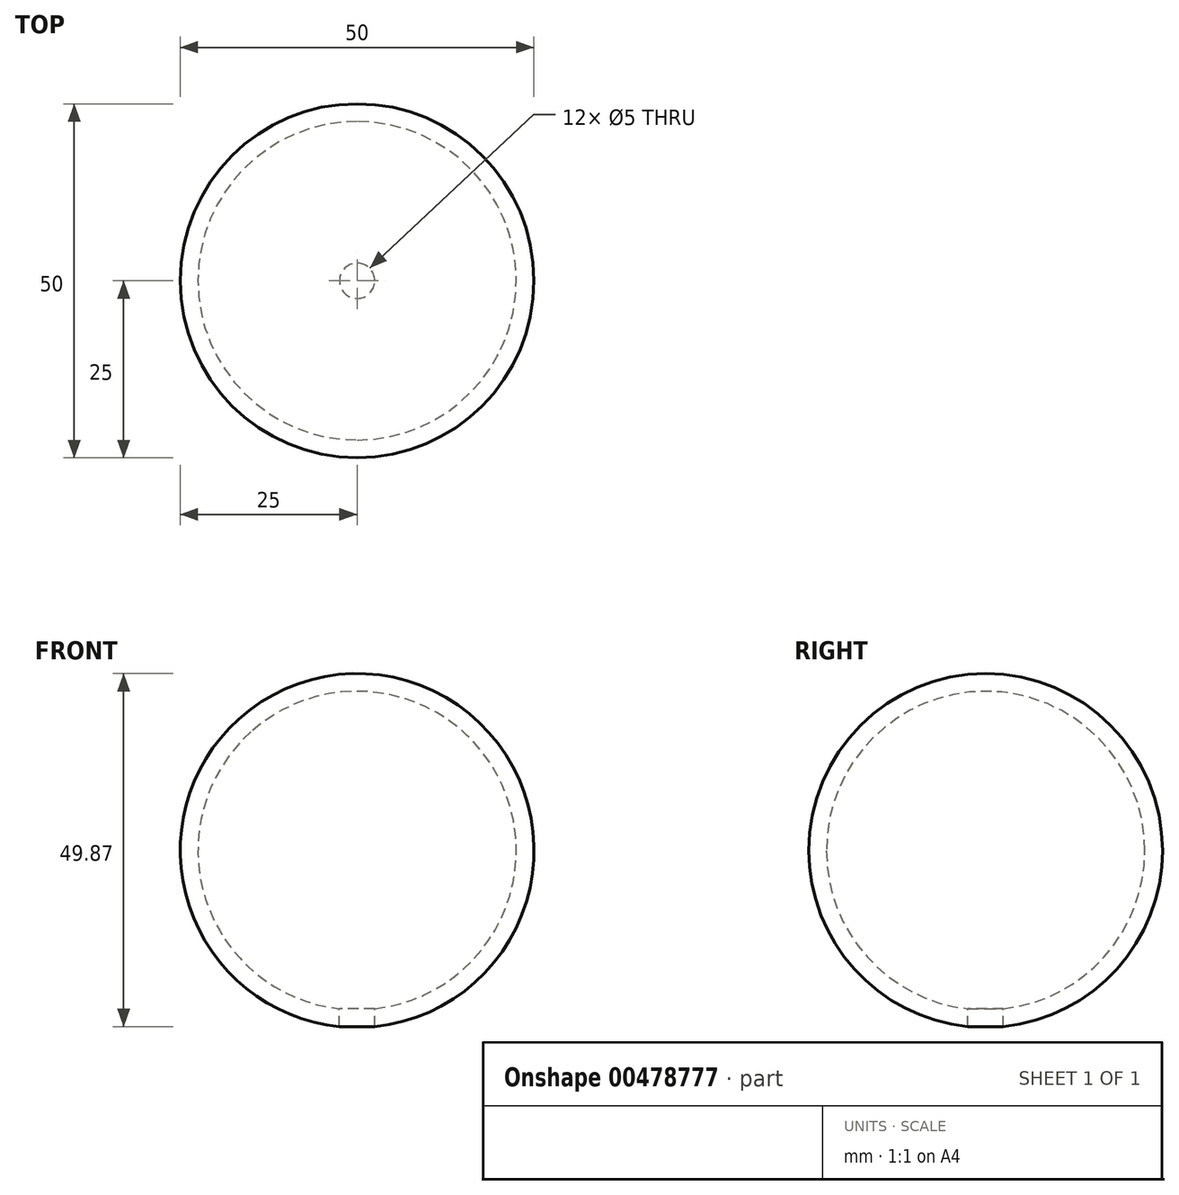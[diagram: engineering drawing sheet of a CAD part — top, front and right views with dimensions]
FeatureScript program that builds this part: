
annotation { "Feature Type Name" : "Feature", "Feature Type Description" : "" }
export const myFeature = defineFeature(function(context is Context, id is Id, definition is map)
    precondition{}
    {
        {
            var Q0;
            Q0=qCreatedBy(makeId("Top.planeOp"),FACE);
            var sketch = newSketch(context, id + "F0", { "sketchPlane" : qUnion([Q0])});
            skLineSegment(sketch, "E0", {"start": v(0, -25) * mm, "end": v(0, 25) * mm});
            skArc(sketch, "E1", {"start": v(0, 25) * mm, "mid": v(-25, 0) * mm, "end": v(0, -25) * mm});
            skLineSegment(sketch, "E2", {"start": v(0, -22.5) * mm, "end": v(0, 22.5) * mm});
            skArc(sketch, "E3", {"start": v(0, 22.5) * mm, "mid": v(-22.5, 0) * mm, "end": v(0, -22.5) * mm});
            skSolve(sketch);
        }
        {
            var Q0;
            {var subQ0=sQuery(id+"F0.wireOp",EDGE,"E1");Q0=makeQuery(id+"F0.imprint","IMPRINT",FACE,{"disambiguationData":[TD([[makeQuery(id+"F0.imprint","IMPRINT",EDGE,{"derivedFrom":subQ0}),1.0]])]});}
            var Q1;
            Q1=sQuery(id+"F0.wireOp",EDGE,"E0");
            revolve(context, id + "F1", {"entities" : qUnion([Q0]), "axis" : qUnion([Q1]), "revolveType" : RevolveType.FULL});
        }
        {
            var Q0;
            Q0=qCreatedBy(makeId("Top.planeOp"),FACE);
            var sketch = newSketch(context, id + "F2", { "sketchPlane" : qUnion([Q0])});
            skCircle(sketch, "E4", {"center": v(0, 0) * mm, "radius": 2.5 * mm});
            skSolve(sketch);
        }
        {
            var Q0;
            Q0 = qSketchRegion(id + "F2", true);
            extrude(context, id + "F3", {"entities" : qUnion([Q0]), "operationType" : NewBodyOperationType.REMOVE, "oppositeDirection" : true, "depth" : 100 * mm});
        }
    });
